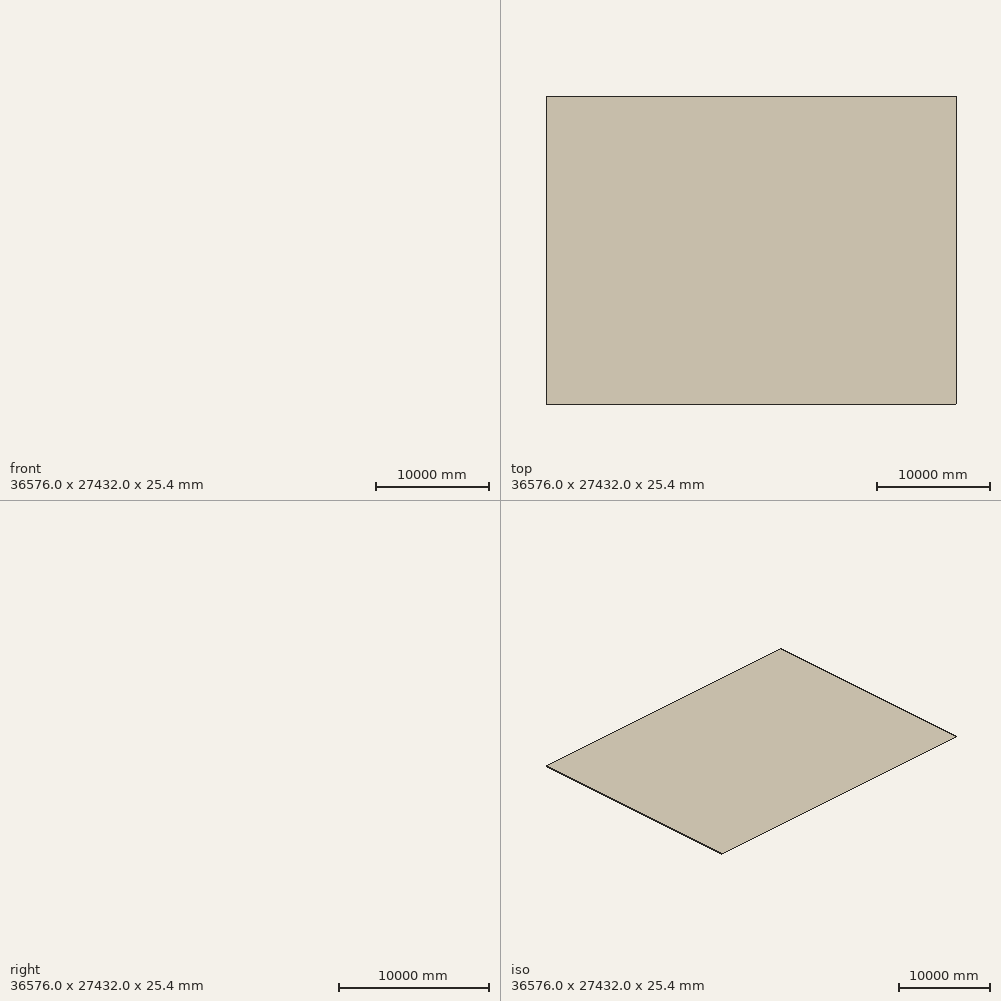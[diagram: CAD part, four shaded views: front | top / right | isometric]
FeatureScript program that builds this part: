
annotation { "Feature Type Name" : "Feature", "Feature Type Description" : "" }
export const myFeature = defineFeature(function(context is Context, id is Id, definition is map)
    precondition{}
    {
        {
            var Q0;
            Q0=qCreatedBy(makeId("Top.planeOp"),FACE);
            var sketch = newSketch(context, id + "F0", { "sketchPlane" : qUnion([Q0])});
            skLineSegment(sketch, "E0.bottom", {"start": v(18288, -13716) * mm, "end": v(-18288, -13716) * mm});
            skLineSegment(sketch, "E0.top", {"start": v(18288, 13716) * mm, "end": v(-18288, 13716) * mm});
            skLineSegment(sketch, "E0.left", {"start": v(18288, -13716) * mm, "end": v(18288, 13716) * mm});
            skLineSegment(sketch, "E0.right", {"start": v(-18288, -13716) * mm, "end": v(-18288, 13716) * mm});
            skPoint(sketch, "E0.middle", {"position": v(0, 0) * mm});
            skSolve(sketch);
        }
        {
            var Q0;
            Q0 = qSketchRegion(id + "F0", true);
            extrude(context, id + "F1", {"entities" : qUnion([Q0]), "depth" : 25.4 * mm, "offsetDistance" : 25.4 * mm});
        }
    });
